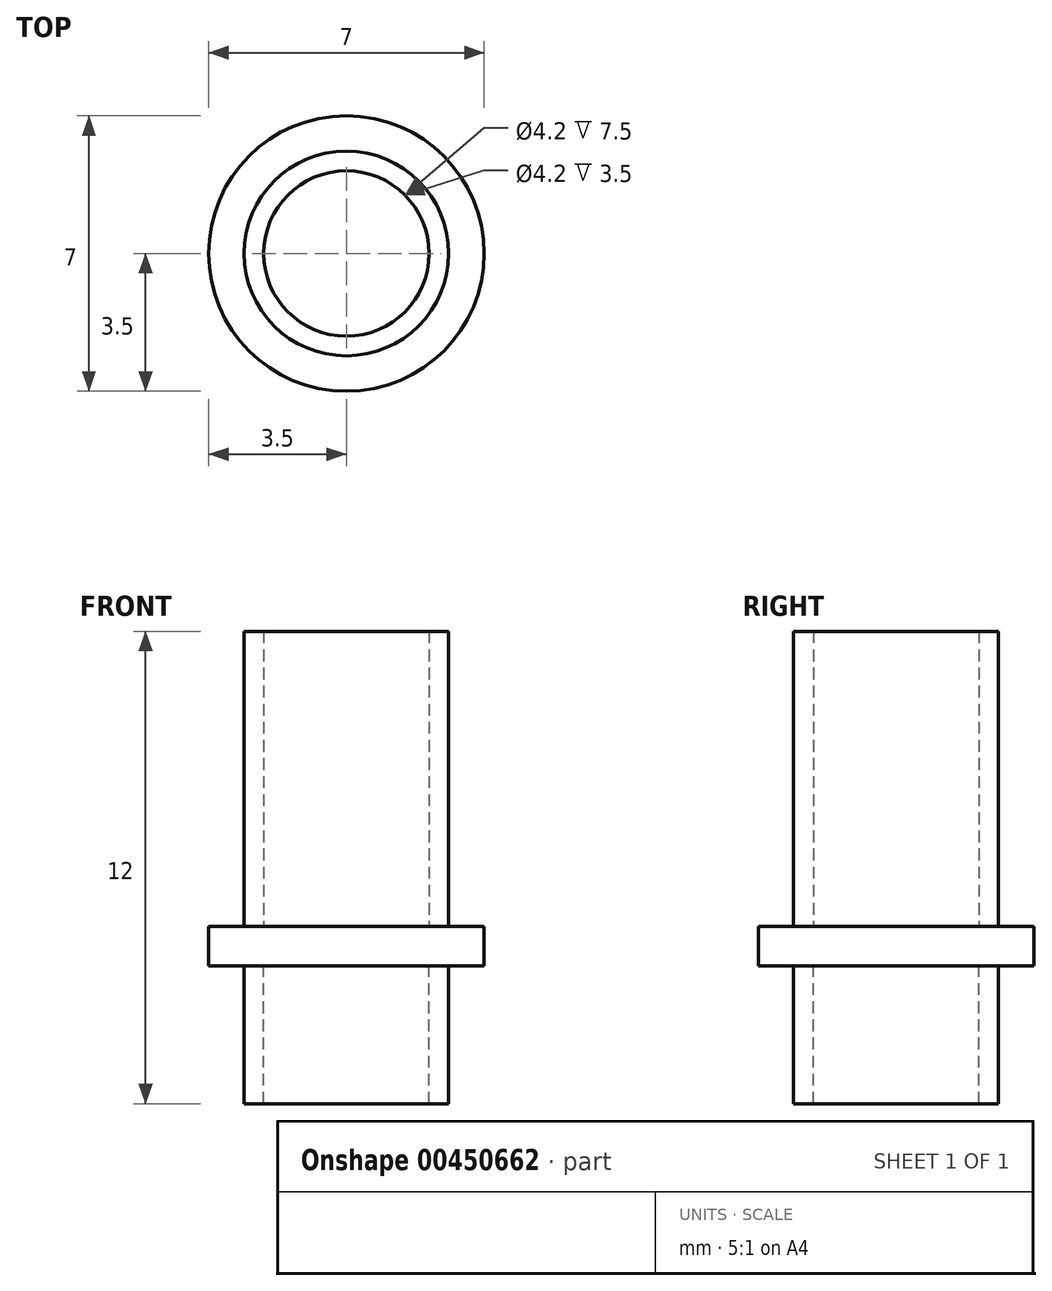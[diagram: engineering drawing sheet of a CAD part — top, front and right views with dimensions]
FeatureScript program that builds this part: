
annotation { "Feature Type Name" : "Feature", "Feature Type Description" : "" }
export const myFeature = defineFeature(function(context is Context, id is Id, definition is map)
    precondition{}
    {
        {
            var Q0;
            Q0=qCreatedBy(makeId("Top.planeOp"),FACE);
            var sketch = newSketch(context, id + "F0", { "sketchPlane" : qUnion([Q0])});
            skCircle(sketch, "E0", {"center": v(0, 0) * mm, "radius": 3.5 * mm});
            skSolve(sketch);
        }
        {
            var Q0;
            Q0 = qSketchRegion(id + "F0", true);
            extrude(context, id + "F1", {"entities" : qUnion([Q0]), "endBound" : BoundingType.SYMMETRIC, "depth" : 1 * mm});
        }
        {
            var Q0;
            Q0=makeQuery(id+"F1.opExtrude","CAP_FACE",FACE,{"disambiguationData":[OSD([sQuery(id+"F0.wireOp",EDGE,"E0")])],"isStart":false});
            var sketch = newSketch(context, id + "F2", { "sketchPlane" : qUnion([Q0])});
            skCircle(sketch, "E1", {"center": v(0, 0) * mm, "radius": 2.6 * mm});
            skCircle(sketch, "E2", {"center": v(0, 0) * mm, "radius": 2.1 * mm});
            skSolve(sketch);
        }
        {
            var Q0;
            Q0 = qSketchRegion(id + "F2", true);
            extrude(context, id + "F3", {"entities" : qUnion([Q0]), "operationType" : NewBodyOperationType.ADD, "depth" : 7.5 * mm});
        }
        {
            var Q0;
            Q0=makeQuery(id+"F1.opExtrude","CAP_FACE",FACE,{"disambiguationData":[OSD([sQuery(id+"F0.wireOp",EDGE,"E0")])],"isStart":true});
            var sketch = newSketch(context, id + "F4", { "sketchPlane" : qUnion([Q0])});
            skCircle(sketch, "E3", {"center": v(0, 0) * mm, "radius": 2.6 * mm});
            skCircle(sketch, "E4", {"center": v(0, 0) * mm, "radius": 2.1 * mm});
            skSolve(sketch);
        }
        {
            var Q0;
            Q0 = qSketchRegion(id + "F4", true);
            extrude(context, id + "F5", {"entities" : qUnion([Q0]), "operationType" : NewBodyOperationType.ADD, "depth" : 3.5 * mm});
        }
    });
